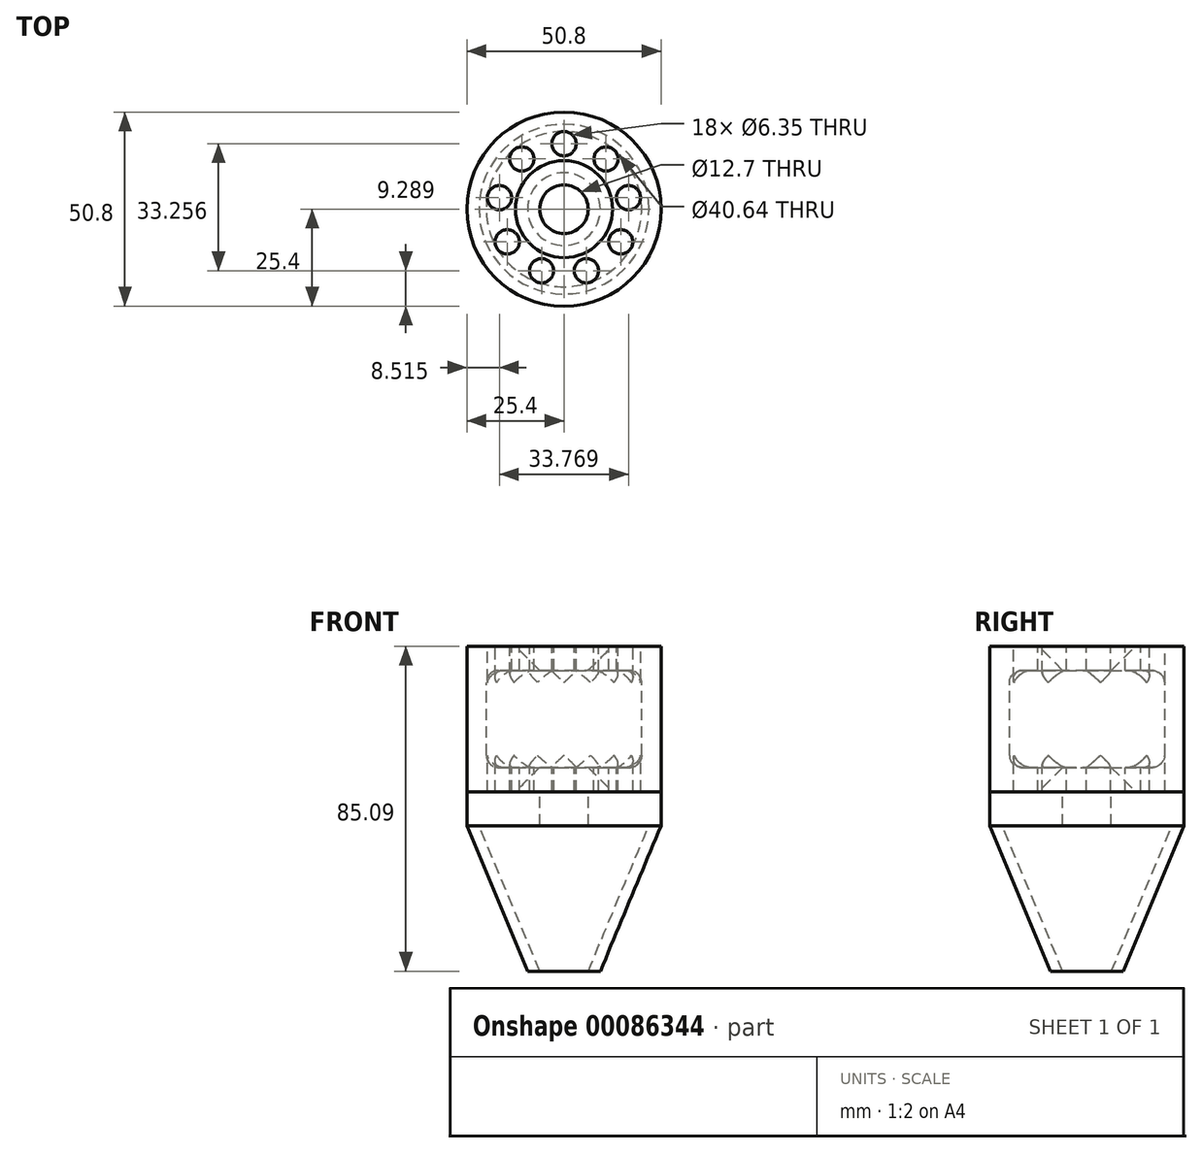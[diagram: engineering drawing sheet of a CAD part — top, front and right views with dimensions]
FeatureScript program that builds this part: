
annotation { "Feature Type Name" : "Feature", "Feature Type Description" : "" }
export const myFeature = defineFeature(function(context is Context, id is Id, definition is map)
    precondition{}
    {
        {
            var Q0;
            Q0=qCreatedBy(makeId("Top.planeOp"),FACE);
            cPlane(context, id + "F0", {"entities" : qUnion([Q0]), "cplaneType" : CPlaneType.OFFSET, "offset" : 38.1 * mm, "width" : 152.4 * mm, "height" : 152.4 * mm});
        }
        {
            var Q0;
            Q0=qCreatedBy(id+"F0.planeOp",FACE);
            var sketch = newSketch(context, id + "F1", { "sketchPlane" : qUnion([Q0])});
            skCircle(sketch, "E0", {"center": v(0, 0) * mm, "radius": 25.4 * mm});
            skSolve(sketch);
        }
        {
            var Q0;
            Q0=qCreatedBy(makeId("Top.planeOp"),FACE);
            var sketch = newSketch(context, id + "F2", { "sketchPlane" : qUnion([Q0])});
            skCircle(sketch, "E1", {"center": v(0, 0) * mm, "radius": 9.53 * mm});
            skSolve(sketch);
        }
        {
            var Q0;
            Q0=makeQuery(id+"F1.imprint","IMPRINT",FACE,{"disambiguationData":[TD([[makeQuery(id+"F1.imprint","IMPRINT",EDGE,{"derivedFrom":sQuery(id+"F1.wireOp",EDGE,"E0")}),1.0]])]});
            var Q1;
            Q1=makeQuery(id+"F2.imprint","IMPRINT",FACE,{"disambiguationData":[TD([[makeQuery(id+"F2.imprint","IMPRINT",EDGE,{"derivedFrom":sQuery(id+"F2.wireOp",EDGE,"E1")}),1.0]])]});
            loft(context, id + "F3", {"sheetProfilesArray" : [{ "sheetProfileEntities" : qUnion([Q0]) }, { "sheetProfileEntities" : qUnion([Q1]) }]});
        }
        {
            var Q0;
            Q0=makeQuery(id+"F1.imprint","IMPRINT",FACE,{"disambiguationData":[TD([[makeQuery(id+"F1.imprint","IMPRINT",EDGE,{"derivedFrom":sQuery(id+"F1.wireOp",EDGE,"E0")}),1.0]])]});
            var sketch = newSketch(context, id + "F4", { "sketchPlane" : qUnion([Q0])});
            skCircle(sketch, "E2", {"center": v(0, 0) * mm, "radius": 22.23 * mm});
            skSolve(sketch);
        }
        {
            var Q0;
            Q0=makeQuery(id+"F2.imprint","IMPRINT",FACE,{"disambiguationData":[TD([[makeQuery(id+"F2.imprint","IMPRINT",EDGE,{"derivedFrom":sQuery(id+"F2.wireOp",EDGE,"E1")}),1.0]])]});
            var sketch = newSketch(context, id + "F5", { "sketchPlane" : qUnion([Q0])});
            skCircle(sketch, "E3", {"center": v(0, 0) * mm, "radius": 6.35 * mm});
            skSolve(sketch);
        }
        {
            var Q1;
            Q1=makeQuery(id+"F4.imprint","IMPRINT",FACE,{"disambiguationData":[TD([[makeQuery(id+"F4.imprint","IMPRINT",EDGE,{"derivedFrom":sQuery(id+"F4.wireOp",EDGE,"E2")}),1.0]])]});
            var Q2;
            Q2=makeQuery(id+"F5.imprint","IMPRINT",FACE,{"disambiguationData":[TD([[makeQuery(id+"F5.imprint","IMPRINT",EDGE,{"derivedFrom":sQuery(id+"F5.wireOp",EDGE,"E3")}),1.0]])]});
            loft(context, id + "F6", {"operationType" : NewBodyOperationType.REMOVE, "sheetProfilesArray" : [{ "sheetProfileEntities" : qUnion([Q1]) }, { "sheetProfileEntities" : qUnion([Q2]) }]});
        }
        {
            var Q0;
            Q0=makeQuery(id+"F1.imprint","IMPRINT",FACE,{"disambiguationData":[TD([[makeQuery(id+"F1.imprint","IMPRINT",EDGE,{"derivedFrom":sQuery(id+"F1.wireOp",EDGE,"E0")}),1.0]])]});
            extrude(context, id + "F7", {"entities" : qUnion([Q0]), "operationType" : NewBodyOperationType.ADD, "depth" : 8.9 * mm});
        }
        {
            var Q0;
            Q0=makeQuery(id+"F7.opExtrude","CAP_FACE",FACE,{"disambiguationData":[OSD([sQuery(id+"F1.wireOp",EDGE,"E0")])],"isStart":false});
            var sketch = newSketch(context, id + "F8", { "sketchPlane" : qUnion([Q0])});
            skCircle(sketch, "E4", {"center": v(0, 0) * mm, "radius": 6.35 * mm});
            skSolve(sketch);
        }
        {
            var Q0;
            Q0 = qSketchRegion(id + "F8", true);
            extrude(context, id + "F9", {"entities" : qUnion([Q0]), "operationType" : NewBodyOperationType.REMOVE, "endBound" : BoundingType.UP_TO_NEXT, "oppositeDirection" : true, "depth" : 25.4 * mm});
        }
        {
            var Q0;
            Q0=makeQuery(id+"F8.imprint","IMPRINT",FACE,{"disambiguationData":[TD([[makeQuery(id+"F8.imprint","IMPRINT",EDGE,{"derivedFrom":sQuery(id+"F8.wireOp",EDGE,"E4")}),-1.0]])]});
            extrude(context, id + "F10", {"entities" : qUnion([Q0]), "depth" : 38.1 * mm});
        }
        {
            var Q0;
            Q0=qCreatedBy(makeId("Front.planeOp"),FACE);
            var sketch = newSketch(context, id + "F11", { "sketchPlane" : qUnion([Q0])});
            skLineSegment(sketch, "E5.bottom", {"start": v(17.14, 78.74) * mm, "end": v(0, 78.74) * mm});
            skLineSegment(sketch, "E5.top", {"start": v(17.15, 53.34) * mm, "end": v(0, 53.34) * mm});
            skLineSegment(sketch, "E5.left", {"start": v(20.32, 75.57) * mm, "end": v(20.32, 56.52) * mm});
            skLineSegment(sketch, "E5.right", {"start": v(0, 78.74) * mm, "end": v(0, 53.34) * mm});
            skPoint(sketch, "E6.visualSharp", {"position": v(20.32, 78.74) * mm});
            skArc(sketch, "E6.filletArc", {"start": v(20.32, 75.57) * mm, "mid": v(19.4, 77.81) * mm, "end": v(17.14, 78.74) * mm});
            skPoint(sketch, "E7.visualSharp", {"position": v(20.32, 53.34) * mm});
            skArc(sketch, "E7.filletArc", {"start": v(17.15, 53.34) * mm, "mid": v(19.4, 54.27) * mm, "end": v(20.32, 56.52) * mm});
            skSolve(sketch);
        }
        {
            var Q0;
            Q0 = qSketchRegion(id + "F11", true);
            var Q1;
            Q1=makeQuery(id+"F10.opExtrude","CAP_EDGE",EDGE,{"disambiguationData":[OSD([sQuery(id+"F1.wireOp",EDGE,"E0")])],"isStart":false});
            revolve(context, id + "F12", {"operationType" : NewBodyOperationType.REMOVE, "entities" : qUnion([Q0]), "axis" : qUnion([Q1]), "revolveType" : RevolveType.FULL, "oppositeDirection" : true});
        }
        {
            var Q0;
            Q0=makeQuery(id+"F10.opExtrude","CAP_EDGE",EDGE,{"disambiguationData":[OSD([sQuery(id+"F8.wireOp",EDGE,"E4")])],"isStart":true});
            var Q1;
            Q1=makeQuery(id+"F10.opExtrude","CAP_EDGE",EDGE,{"disambiguationData":[OSD([sQuery(id+"F8.wireOp",EDGE,"E4")])],"isStart":false});
            chamfer(context, id + "F13", {"entities" : qUnion([Q0, Q1]), "width" : 6.35 * mm, "tangentPropagation" : true});
        }
        {
            var Q0;
            Q0=makeQuery(id+"F10.opExtrude","CAP_FACE",FACE,{"disambiguationData":[OSD([sQuery(id+"F1.wireOp",EDGE,"E0"),sQuery(id+"F8.wireOp",EDGE,"E4")])],"isStart":false});
            var sketch = newSketch(context, id + "F14", { "sketchPlane" : qUnion([Q0])});
            skCircle(sketch, "E8", {"center": v(0, 17.14) * mm, "radius": 3.18 * mm});
            skCircle(sketch, "E9.1.0", {"center": v(-11.02, 13.13) * mm, "radius": 3.18 * mm});
            skCircle(sketch, "E9.2.0", {"center": v(-16.88, 2.98) * mm, "radius": 3.18 * mm});
            skCircle(sketch, "E9.3.0", {"center": v(-14.85, -8.57) * mm, "radius": 3.18 * mm});
            skCircle(sketch, "E9.4.0", {"center": v(-5.86, -16.11) * mm, "radius": 3.18 * mm});
            skCircle(sketch, "E9.5.0", {"center": v(5.86, -16.11) * mm, "radius": 3.18 * mm});
            skCircle(sketch, "E9.6.0", {"center": v(14.85, -8.57) * mm, "radius": 3.18 * mm});
            skCircle(sketch, "E9.7.0", {"center": v(16.88, 2.98) * mm, "radius": 3.18 * mm});
            skCircle(sketch, "E9.8.0", {"center": v(11.02, 13.13) * mm, "radius": 3.18 * mm});
            skPoint(sketch, "E9.center", {"position": v(0, 0) * mm});
            skSolve(sketch);
        }
        {
            var Q0;
            Q0 = qSketchRegion(id + "F14", true);
            var Q1;
            Q1=makeQuery(id+"F10.opExtrude","CAP_FACE",FACE,{"disambiguationData":[OSD([sQuery(id+"F1.wireOp",EDGE,"E0"),sQuery(id+"F8.wireOp",EDGE,"E4")])],"isStart":true});
            extrude(context, id + "F15", {"entities" : qUnion([Q0]), "operationType" : NewBodyOperationType.REMOVE, "endBound" : BoundingType.UP_TO_SURFACE, "oppositeDirection" : true, "endBoundEntityFace" : qUnion([Q1]), "depth" : 25.4 * mm});
        }
    });
